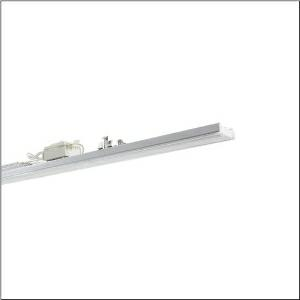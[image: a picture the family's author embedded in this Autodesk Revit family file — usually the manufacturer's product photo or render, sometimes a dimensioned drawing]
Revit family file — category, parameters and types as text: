
# Revit family: licross_21_recessed_mo_52tl11dn68xg
name_source: partatom
category: Lighting Fixtures
units: mm (PartAtom-declared; Revit-internal decimal feet)

## family parameters
Cut with Voids When Loaded = No
Host = Face
Light Source = No
Part Type = Normal
Room Calculation Point = No
Round Connector Dimension = Use Diameter
Shared = No

## types (1)
- --- (1 x LED, 8000 lm, 46.3 W, 6500K)
    Apparent Load = 46 VA
    CIE Flux Codes = 89 96 99 100 100
    Color Rendering = 80
    Color Temperature = 6500K
    Default Elevation = 1800 mm
    Description = Licross 21 Recessed MO, luminaire insert, of sheet steel, galvanised, coil coated, white, length: 1.500mm, width: 66mm, height: 67mm, LED rated luminous flux: 8.000lm, light colour: 865, SDCM (Standard Deviation of Colour Matching)MacAdam ≤ 3 SDCM (initial), control gear: DALI 2, with plug, 5-pole, with phase selection, mains connection: 220..240V, AC, 50/60Hz, rated input power: 46W, internal wiring halogen-free, primary light control with lens, of plastic, primary optical cover: cover, of PMMA, light emission: direct distribution, primary light characteristic: symmetric, protection rating (complete): IP40, insulation class (complete): insulation class I (protective earthing), certification: CE, ENEC, VDE, UKCA, protection symbol: D if used in an environment without relevant dust loads with corresponding accessories, impact resistance: IK06, permissible ambient temperature for indoor applications: -25..+40°C, corresponds to IFS (International Featured Standards) requirements for safety and quality in the food industry, reducing of maximum allowable ambient temperature of 5°C with ceiling mounting, LABS conformity tested according to VDMA 24364:2018-05, The light source and the operating device comply with the requirements of the Ecodesign Regulation (EU) 2019/2020 and are replaceable in accordance with this regulation, packaging unit: 1 piece
    Height = 58 mm
    Lamp = 1 x LED
    Lamp Light Flux = 8000 lm
    Lamp Power = 46.3 W
    Lamp count = 1
    Length = 1500 mm
    Luminous efficacy = 173 lm/W
    Manufacturer = Siteco
    ModVariant = No
    Model = 52TL11DN68XG
    Mounting Place = Ceiling
    Mounting Type = Pendant
    Number of Poles = 1
    OnlyDefault = Yes
    Power Factor = 1
    Product Name = Licross 21 Recessed MO
    Product group = luminaire insert | ceiling pendant
    ProductGroupID = 901
    Protection Class = Protection class I
    Protection Degree = IP 40
    RLX_Detail_Level = 1
    RLX_Emergency_Light_Flux = 0 lm
    RLX_Emergency_Type = 0
    RLX_Emergency_Type_DB = No
    RlxData = <blob elided: 24801 chars, md5=c4d1e7d1>
    Socket = socket
    Standby Power = 0 W
    System Light Flux = 8000 lm
    System Power = 46 W
    Type Comments = factory setting: luminous flux: 100 % | dim-lin: 254 | 311 mA
    Type Image = l_1296930.jpg
    URL = http://relux.com
    VarID = @adj_030027
    Voltage = 0 V
    Weight = 0.00 kg
    Width = 66 mm

## geometry (parser evidence)
native form markers: Blend x4, Sweep x12
no freeform markers — native parametric forms only
